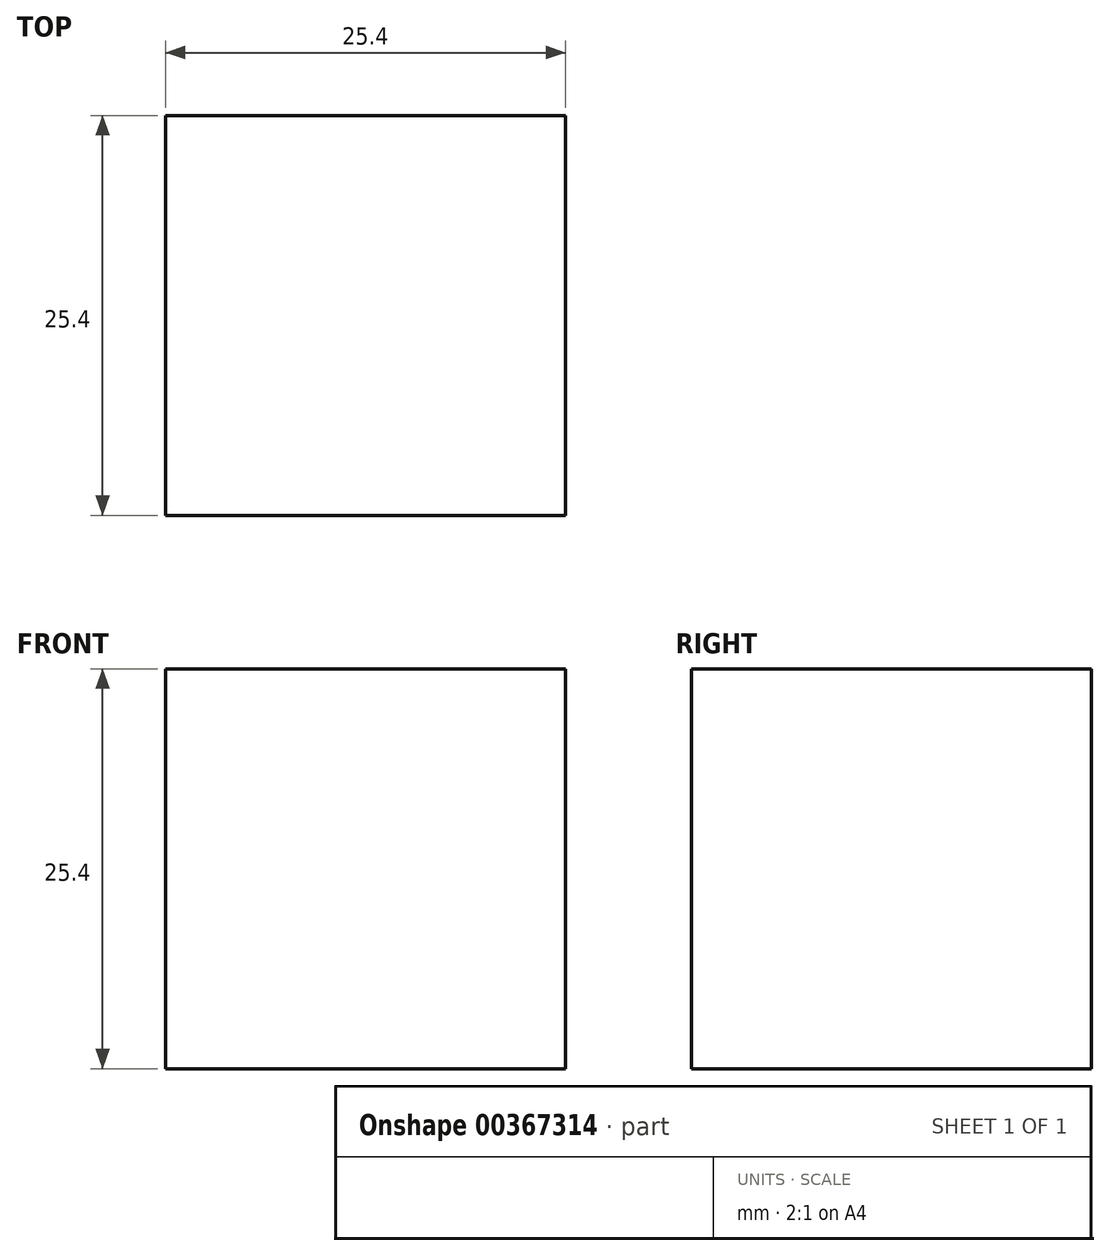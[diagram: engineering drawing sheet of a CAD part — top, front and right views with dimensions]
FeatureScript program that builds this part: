
annotation { "Feature Type Name" : "Feature", "Feature Type Description" : "" }
export const myFeature = defineFeature(function(context is Context, id is Id, definition is map)
    precondition{}
    {
        {
            var Q0;
            Q0=qCreatedBy(makeId("Top.planeOp"),FACE);
            var sketch = newSketch(context, id + "F0", { "sketchPlane" : qUnion([Q0])});
            skLineSegment(sketch, "E0.bottom", {"start": v(-12.7, 12.7) * mm, "end": v(12.7, 12.7) * mm});
            skLineSegment(sketch, "E0.top", {"start": v(-12.7, -12.7) * mm, "end": v(12.7, -12.7) * mm});
            skLineSegment(sketch, "E0.left", {"start": v(-12.7, 12.7) * mm, "end": v(-12.7, -12.7) * mm});
            skLineSegment(sketch, "E0.right", {"start": v(12.7, 12.7) * mm, "end": v(12.7, -12.7) * mm});
            skSolve(sketch);
        }
        {
            var Q0;
            Q0=makeQuery(id+"F0.imprint","IMPRINT",FACE,{"disambiguationData":[TD([[makeQuery(id+"F0.imprint","IMPRINT",EDGE,{"derivedFrom":sQuery(id+"F0.wireOp",EDGE,"E0.bottom")}),-1.0]])]});
            extrude(context, id + "F1", {"entities" : qUnion([Q0]), "depth" : 25.4 * mm});
        }
    });
